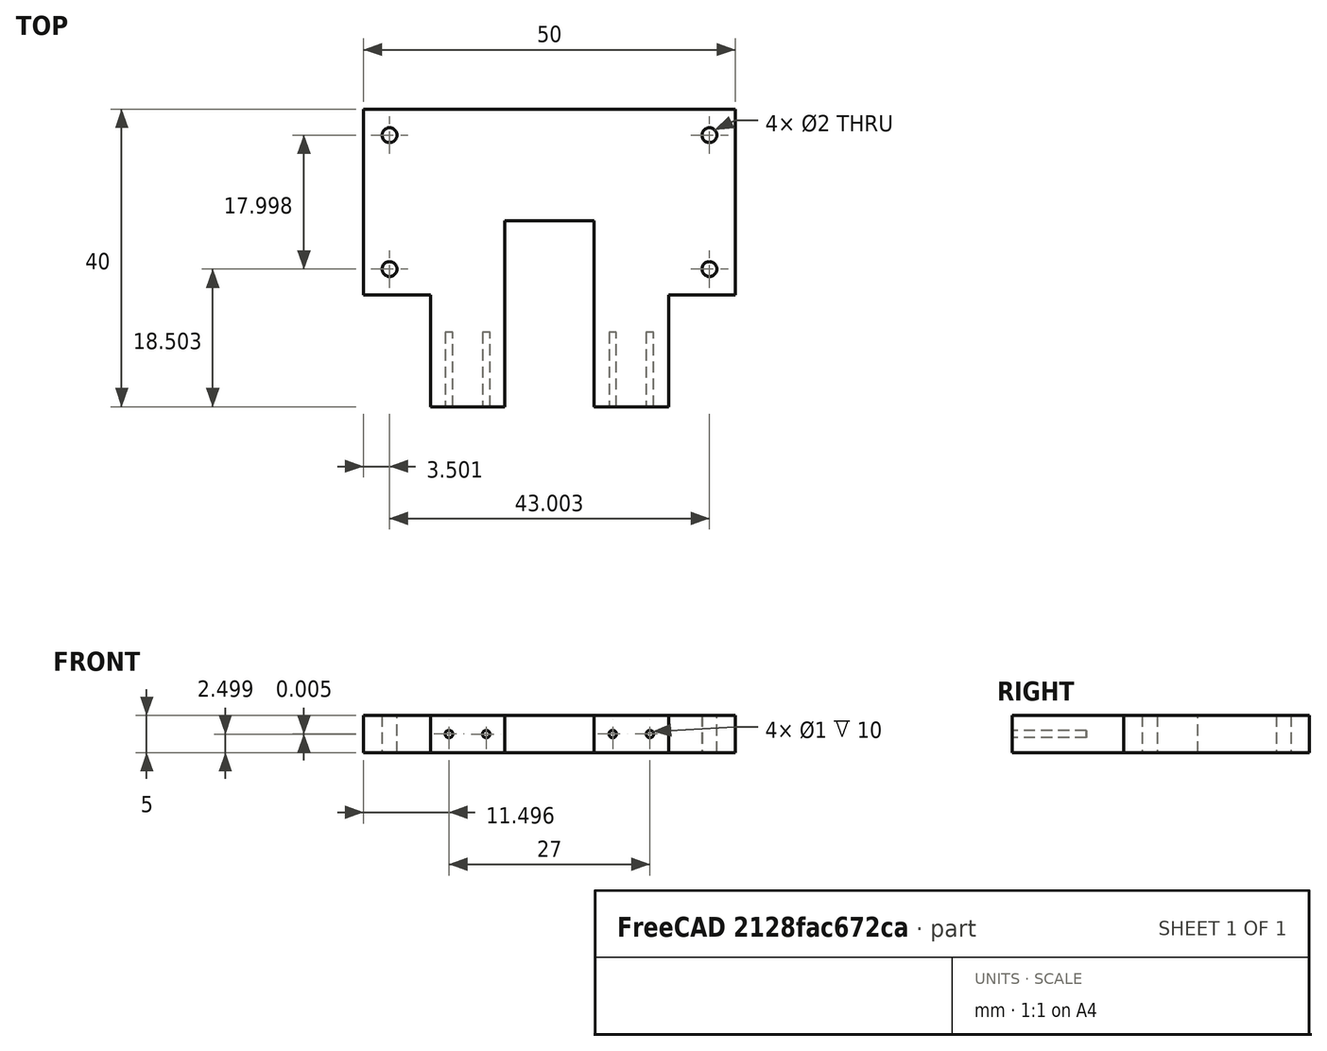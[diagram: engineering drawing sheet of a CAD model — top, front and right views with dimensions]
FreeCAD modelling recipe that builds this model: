
FCSTD DOCUMENT  (FreeCAD 1.0R39109 (Git))
Label: ultrasonic_holder
License: All rights reserved
LicenseURL: https://en.wikipedia.org/wiki/All_rights_reserved
objects: Sketcher::SketchObject×3, PartDesign::Body×2, PartDesign::Pad×1, PartDesign::Pocket×1
note: 14 computed .brp shape members not serialized (recipe doc carries the construction recipe); baked Part::Feature solids carry a one-line shape summary decoded from their .brp

FEATURE [PartDesign::Body] Body
  AllowCompound = false
  Origin = -> Origin
FEATURE [Sketcher::SketchObject] Sketch
  ArcFitTolerance = 1e-06
  AttachmentSupport = -> [XZ_Plane001]
  FullyConstrained = true
  MakeInternals = false
  MapMode = 5
  Placement = pos=(0,0,0) rot=(1,0,0;1.5708rad)
FEATURE [Sketcher::SketchObject] Sketch001
  ArcFitTolerance = 1e-06
  AttachmentSupport = -> [XY_Plane001]
  FullyConstrained = false
  MakeInternals = false
  MapMode = 5
  sketch-geometry (24):
    g0: LineSegment StartX=9 StartY=0 StartZ=0 EndX=9 EndY=15 EndZ=0
    g1: LineSegment StartX=9 StartY=15 StartZ=0 EndX=0 EndY=15 EndZ=0
    g2: LineSegment StartX=50 StartY=15 StartZ=0 EndX=41 EndY=15 EndZ=0
    g3: LineSegment StartX=41 StartY=15 StartZ=0 EndX=41 EndY=0 EndZ=0
    g4: LineSegment StartX=9 StartY=0 StartZ=0 EndX=19 EndY=0 EndZ=0
    g5: LineSegment StartX=41 StartY=0 StartZ=0 EndX=31 EndY=0 EndZ=0
    g6: LineSegment StartX=0 StartY=40 StartZ=0 EndX=50 EndY=40 EndZ=0
    g7: LineSegment StartX=0 StartY=40 StartZ=0 EndX=0 EndY=15 EndZ=0
    g8: LineSegment StartX=50 StartY=40 StartZ=0 EndX=50 EndY=15 EndZ=0
    g9: LineSegment StartX=31 StartY=25 StartZ=0 EndX=19 EndY=25 EndZ=0
    g10: LineSegment StartX=19 StartY=0 StartZ=0 EndX=19 EndY=25 EndZ=0
    g11: LineSegment StartX=31 StartY=0 StartZ=0 EndX=31 EndY=25 EndZ=0
    g12: GeomPoint X=2.49801 Y=17.5024 Z=0
    g13: GeomPoint X=2.49801 Y=37.4994 Z=0
    g14: GeomPoint X=47.4974 Y=37.4994 Z=0
    g15: GeomPoint X=47.4974 Y=17.5006 Z=0
    g16: GeomPoint X=46.4967 Y=18.5032 Z=0
    g17: GeomPoint X=3.50056 Y=18.5032 Z=0
    g18: GeomPoint X=3.50056 Y=36.5014 Z=0
    g19: GeomPoint X=46.504 Y=36.5014 Z=0
    g20: Circle CenterX=46.504 CenterY=36.5014 CenterZ=0 NormalX=0 NormalY=0 NormalZ=1 AngleXU=0 Radius=1
    g21: Circle CenterX=3.50056 CenterY=36.5014 CenterZ=0 NormalX=0 NormalY=0 NormalZ=1 AngleXU=0 Radius=1
    g22: Circle CenterX=3.50056 CenterY=18.5032 CenterZ=0 NormalX=0 NormalY=0 NormalZ=1 AngleXU=0 Radius=1
    g23: Circle CenterX=46.4967 CenterY=18.5032 CenterZ=0 NormalX=0 NormalY=0 NormalZ=1 AngleXU=0 Radius=1
  constraints (33):
    c: Vertical(g0)
    c: PointOnObject(g0,g-1)
    c: Coincident(g1,g0)
    c: PointOnObject(g1,g-2)
    c: Horizontal(g1)
    c: Horizontal(g2)
    c: Coincident(g3,g2)
    c: PointOnObject(g3,g-1)
    c: Vertical(g3)
    c: Coincident(g4,g0)
    c: PointOnObject(g4,g-1)
    c: Coincident(g5,g3)
    c: PointOnObject(g5,g-1)
    c: Horizontal(g6)
    c: Coincident(g7,g6)
    c: Coincident(g7,g1)
    c: Vertical(g7)
    c: Coincident(g8,g6)
    c: Coincident(g8,g2)
    c: Coincident(g10,g4)
    c: Coincident(g10,g9)
    c: Vertical(g10)
    c: Coincident(g11,g5)
    c: Coincident(g11,g9)
    c: Vertical(g11)
    c: Diameter(g20) = 2
    c: Coincident(g20,g19)
    c: Diameter(g21) = 2
    c: Coincident(g21,g18)
    c: Diameter(g22) = 2
    c: Coincident(g22,g17)
    c: Diameter(g23) = 2
    c: Coincident(g23,g16)
FEATURE [PartDesign::Pad] Pad
  Direction = (0,0,1)
  Length = 5
  Length2 = 10
  Profile = -> Sketch001
  ReferenceAxis = -> Sketch001 [N_Axis]
  Refine = true
  Suppressed = false
  Type = 0
FEATURE [Sketcher::SketchObject] Sketch002
  ArcFitTolerance = 1e-06
  AttachmentSupport = -> [Pad]
  FullyConstrained = false
  MakeInternals = false
  MapMode = 5
  Placement = pos=(0,0,0) rot=(1,0,0;1.5708rad)
  sketch-geometry (11):
    g0: GeomPoint X=8.99759 Y=2.49897 Z=0
    g1: GeomPoint X=30.9972 Y=2.50268 Z=0
    g2: GeomPoint X=40.9957 Y=2.49992 Z=0
    g3: GeomPoint X=11.4962 Y=2.50362 Z=0
    g4: GeomPoint X=16.5026 Y=2.49858 Z=0
    g5: GeomPoint X=33.4998 Y=2.50362 Z=0
    g6: GeomPoint X=38.4961 Y=2.50362 Z=0
    g7: Circle CenterX=38.4961 CenterY=2.50362 CenterZ=0 NormalX=0 NormalY=0 NormalZ=1 AngleXU=0 Radius=0.5
    g8: Circle CenterX=33.4998 CenterY=2.50362 CenterZ=0 NormalX=0 NormalY=0 NormalZ=1 AngleXU=0 Radius=0.5
    g9: Circle CenterX=16.5026 CenterY=2.49858 CenterZ=0 NormalX=0 NormalY=0 NormalZ=1 AngleXU=0 Radius=0.5
    g10: Circle CenterX=11.4962 CenterY=2.50362 CenterZ=0 NormalX=0 NormalY=0 NormalZ=1 AngleXU=0 Radius=0.5
  constraints (8):
    c: Diameter(g7) = 1
    c: Coincident(g7,g6)
    c: Diameter(g8) = 1
    c: Coincident(g8,g5)
    c: Diameter(g9) = 1
    c: Coincident(g9,g4)
    c: Diameter(g10) = 1
    c: Coincident(g10,g3)
FEATURE [PartDesign::Pocket] Pocket
  BaseFeature = -> Pad
  Direction = (0,1,-2e-16)
  Length = 10
  Length2 = 5
  Profile = -> Sketch002
  ReferenceAxis = -> Sketch002 [N_Axis]
  Refine = true
  Suppressed = false
  Type = 0
FEATURE [PartDesign::Body] Body001
  AllowCompound = false
  Group = -> [Sketch,Sketch001,Pad,Sketch002,Pocket]
  Origin = -> Origin001
  Tip = -> Pocket
